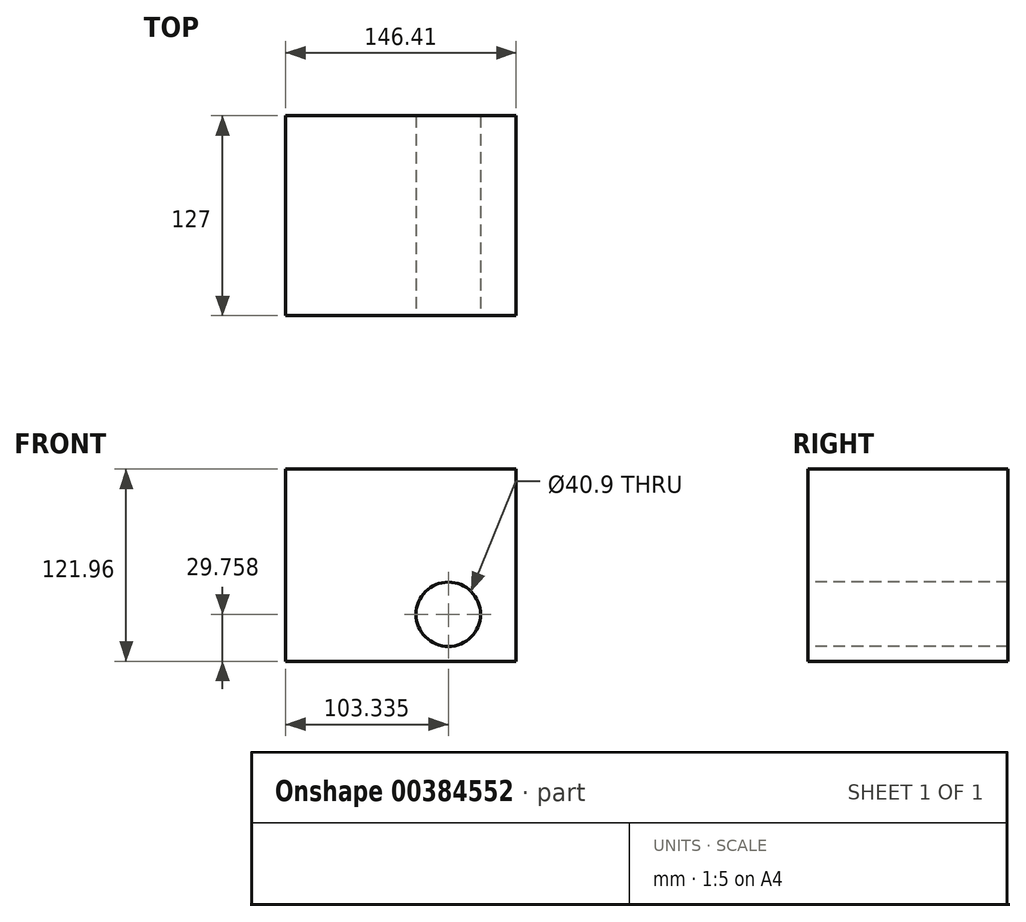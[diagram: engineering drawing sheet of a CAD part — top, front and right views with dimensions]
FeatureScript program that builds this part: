
annotation { "Feature Type Name" : "Feature", "Feature Type Description" : "" }
export const myFeature = defineFeature(function(context is Context, id is Id, definition is map)
    precondition{}
    {
        {
            var Q0;
            Q0=qCreatedBy(makeId("Front.planeOp"),FACE);
            var sketch = newSketch(context, id + "F0", { "sketchPlane" : qUnion([Q0])});
            skLineSegment(sketch, "E0.bottom", {"start": v(-74.52, 46.42) * mm, "end": v(71.89, 46.42) * mm});
            skLineSegment(sketch, "E0.top", {"start": v(-74.52, -75.54) * mm, "end": v(71.89, -75.54) * mm});
            skLineSegment(sketch, "E0.left", {"start": v(-74.52, 46.42) * mm, "end": v(-74.52, -75.54) * mm});
            skLineSegment(sketch, "E0.right", {"start": v(71.89, 46.42) * mm, "end": v(71.89, -75.54) * mm});
            skSolve(sketch);
        }
        {
            var Q0;
            Q0=makeQuery(id+"F0.imprint","IMPRINT",FACE,{"disambiguationData":[TD([[makeQuery(id+"F0.imprint","IMPRINT",EDGE,{"derivedFrom":sQuery(id+"F0.wireOp",EDGE,"E0.bottom")}),-1.0]])]});
            extrude(context, id + "F1", {"entities" : qUnion([Q0]), "depth" : 127 * mm});
        }
        {
            var Q0;
            Q0=makeQuery(id+"F1.opExtrude","CAP_FACE",FACE,{"disambiguationData":[OSD([sQuery(id+"F0.wireOp",EDGE,"E0.bottom"),sQuery(id+"F0.wireOp",EDGE,"E0.top"),sQuery(id+"F0.wireOp",EDGE,"E0.left"),sQuery(id+"F0.wireOp",EDGE,"E0.right")])],"isStart":true});
            var sketch = newSketch(context, id + "F2", { "sketchPlane" : qUnion([Q0])});
            skCircle(sketch, "E1", {"center": v(-28.82, -45.78) * mm, "radius": 20.45 * mm});
            skSolve(sketch);
        }
        {
            var Q0;
            Q0=makeQuery(id+"F2.imprint","IMPRINT",FACE,{"disambiguationData":[TD([[makeQuery(id+"F2.imprint","IMPRINT",EDGE,{"derivedFrom":sQuery(id+"F2.wireOp",EDGE,"E1")}),-1.0]])]});
            var sketch = newSketch(context, id + "F3", { "sketchPlane" : qUnion([Q0])});
            skPoint(sketch, "E2", {"position": v(-28.06, -46.5) * mm});
            skSolve(sketch);
        }
        {
            var Q0;
            Q0=sQuery(id+"F3.wireOp",VERTEX,"E2");
            var Q1;
            Q1=makeQuery(id+"F1.opExtrude","SWEPT_BODY",BODY,{"disambiguationData":[OSD([sQuery(id+"F0.wireOp",EDGE,"E0.bottom"),sQuery(id+"F0.wireOp",EDGE,"E0.top"),sQuery(id+"F0.wireOp",EDGE,"E0.left"),sQuery(id+"F0.wireOp",EDGE,"E0.right")])]});
            hole(context, id + "F4", {"style" : HoleStyle.SIMPLE, "endStyle" : HoleEndStyle.THROUGH, "holeDiameter" : 25.4 * mm, "isTappedThrough" : true, "tappedDepth" : 12.7 * mm, "tapClearance" : 3, "locations" : qUnion([Q0]), "scope" : qUnion([Q1])});
        }
        {
            var Q0;
            Q0=makeQuery(id+"F1.opExtrude","SWEPT_BODY",BODY,{"disambiguationData":[OSD([sQuery(id+"F0.wireOp",EDGE,"E0.bottom"),sQuery(id+"F0.wireOp",EDGE,"E0.top"),sQuery(id+"F0.wireOp",EDGE,"E0.left"),sQuery(id+"F0.wireOp",EDGE,"E0.right")])]});
            deleteBodies(context, id + "F5", {"entities" : qUnion([Q0])});
        }
        {
            var Q0;
            Q0=makeQuery(id+"F2.imprint","IMPRINT",FACE,{"disambiguationData":[TD([[makeQuery(id+"F2.imprint","IMPRINT",EDGE,{"derivedFrom":sQuery(id+"F2.wireOp",EDGE,"E1")}),-1.0]])]});
            extrude(context, id + "F6", {"entities" : qUnion([Q0]), "depth" : 127 * mm});
        }
    });
